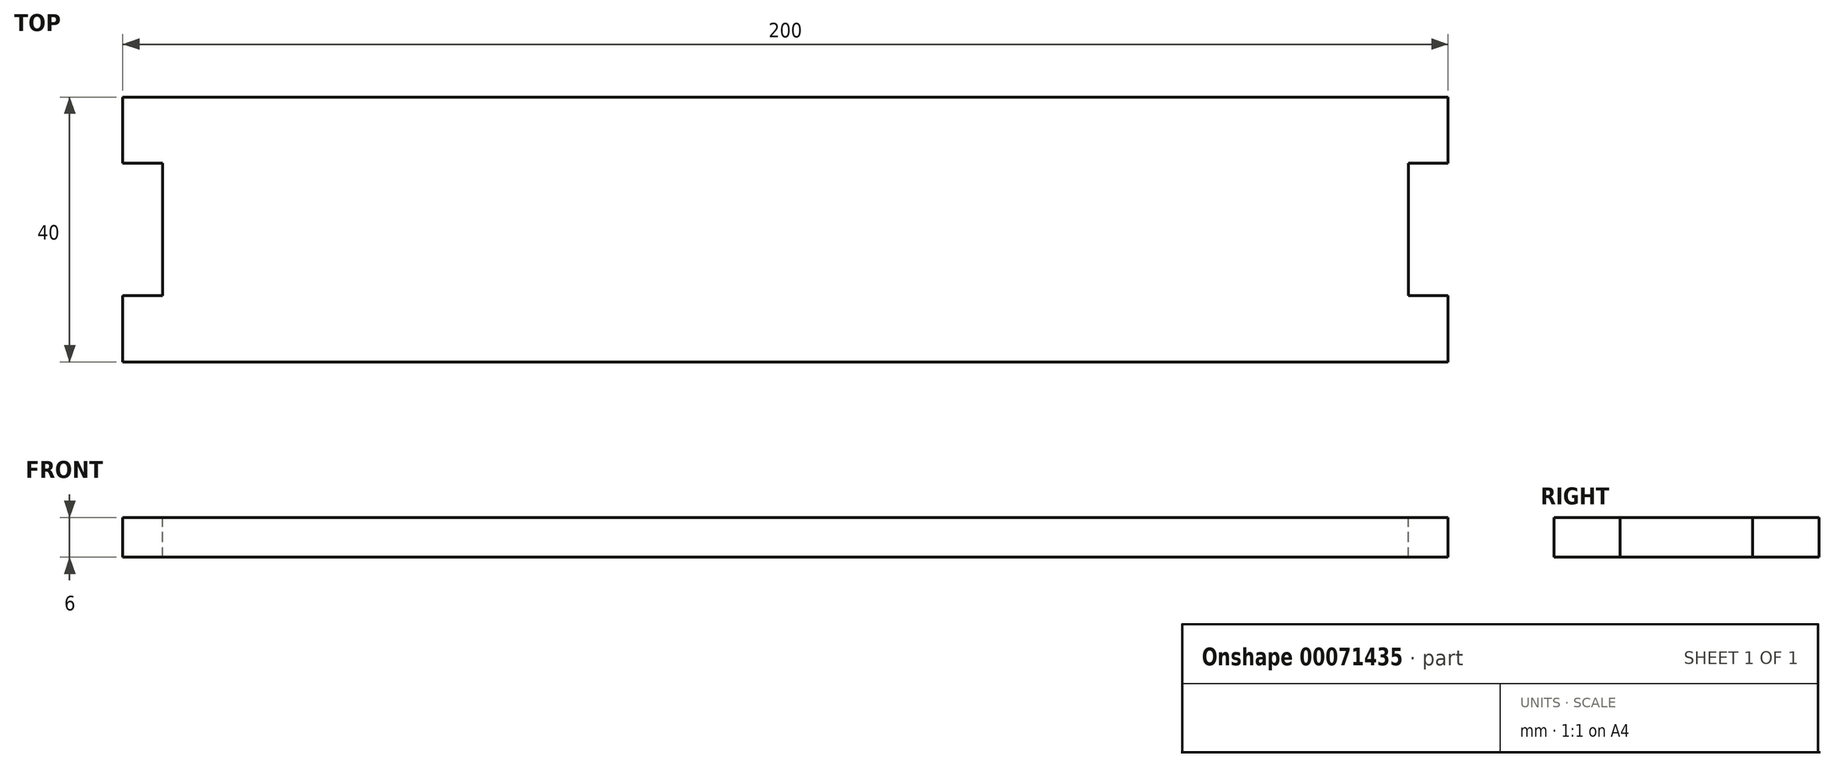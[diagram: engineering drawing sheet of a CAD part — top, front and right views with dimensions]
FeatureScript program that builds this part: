
annotation { "Feature Type Name" : "Feature", "Feature Type Description" : "" }
export const myFeature = defineFeature(function(context is Context, id is Id, definition is map)
    precondition{}
    {
        {
            var Q0;
            Q0=qCreatedBy(makeId("Top.planeOp"),FACE);
            var sketch = newSketch(context, id + "F0", { "sketchPlane" : qUnion([Q0])});
            skLineSegment(sketch, "E0.rect.bottom", {"start": v(100, -20) * mm, "end": v(-100, -20) * mm});
            skLineSegment(sketch, "E0.rect.top", {"start": v(100, 20) * mm, "end": v(-100, 20) * mm});
            skLineSegment(sketch, "E0.rect.left", {"start": v(100, -20) * mm, "end": v(100, 20) * mm});
            skLineSegment(sketch, "E0.rect.right", {"start": v(-100, -20) * mm, "end": v(-100, 20) * mm});
            skPoint(sketch, "E0.rect.middle", {"position": v(0, 0) * mm});
            skSolve(sketch);
        }
        {
            var Q0;
            Q0=makeQuery(id+"F0.imprint","IMPRINT",FACE,{"disambiguationData":[TD([[makeQuery(id+"F0.imprint","IMPRINT",EDGE,{"derivedFrom":sQuery(id+"F0.wireOp",EDGE,"E0.rect.bottom")}),-1.0]])]});
            extrude(context, id + "F1", {"entities" : qUnion([Q0]), "depth" : 6 * mm});
        }
        {
            var Q0;
            Q0=makeQuery(id+"F1.opExtrude","CAP_FACE",FACE,{"disambiguationData":[OSD([sQuery(id+"F0.wireOp",EDGE,"E0.rect.bottom"),sQuery(id+"F0.wireOp",EDGE,"E0.rect.top"),sQuery(id+"F0.wireOp",EDGE,"E0.rect.left"),sQuery(id+"F0.wireOp",EDGE,"E0.rect.right")])],"isStart":false});
            var sketch = newSketch(context, id + "F2", { "sketchPlane" : qUnion([Q0])});
            skLineSegment(sketch, "E1.bottom", {"start": v(-100, 10) * mm, "end": v(-94, 10) * mm});
            skLineSegment(sketch, "E1.top", {"start": v(-100, -10) * mm, "end": v(-94, -10) * mm});
            skLineSegment(sketch, "E1.left", {"start": v(-100, 10) * mm, "end": v(-100, -10) * mm});
            skLineSegment(sketch, "E1.right", {"start": v(-94, 10) * mm, "end": v(-94, -10) * mm});
            skLineSegment(sketch, "E2", {"start": v(0, 20) * mm, "end": v(0, -20) * mm, "construction": true});
            skLineSegment(sketch, "E3.MirrorCS", {"start": v(94, 10) * mm, "end": v(94, -10) * mm});
            skLineSegment(sketch, "E4.MirrorCS", {"start": v(100, 10) * mm, "end": v(100, -10) * mm});
            skLineSegment(sketch, "E5.MirrorCS", {"start": v(100, -10) * mm, "end": v(94, -10) * mm});
            skLineSegment(sketch, "E6.MirrorCS", {"start": v(100, 10) * mm, "end": v(94, 10) * mm});
            skSolve(sketch);
        }
        {
            var Q0;
            Q0=makeQuery(id+"F2.imprint","IMPRINT",FACE,{"disambiguationData":[TD([[makeQuery(id+"F2.imprint","IMPRINT",EDGE,{"derivedFrom":sQuery(id+"F2.wireOp",EDGE,"E3.MirrorCS")}),1.0]])]});
            var Q1;
            Q1=makeQuery(id+"F2.imprint","IMPRINT",FACE,{"disambiguationData":[TD([[makeQuery(id+"F2.imprint","IMPRINT",EDGE,{"derivedFrom":sQuery(id+"F2.wireOp",EDGE,"E1.bottom")}),-1.0]])]});
            extrude(context, id + "F3", {"entities" : qUnion([Q0, Q1]), "operationType" : NewBodyOperationType.REMOVE, "endBound" : BoundingType.UP_TO_NEXT, "oppositeDirection" : true, "depth" : 25 * mm});
        }
    });
